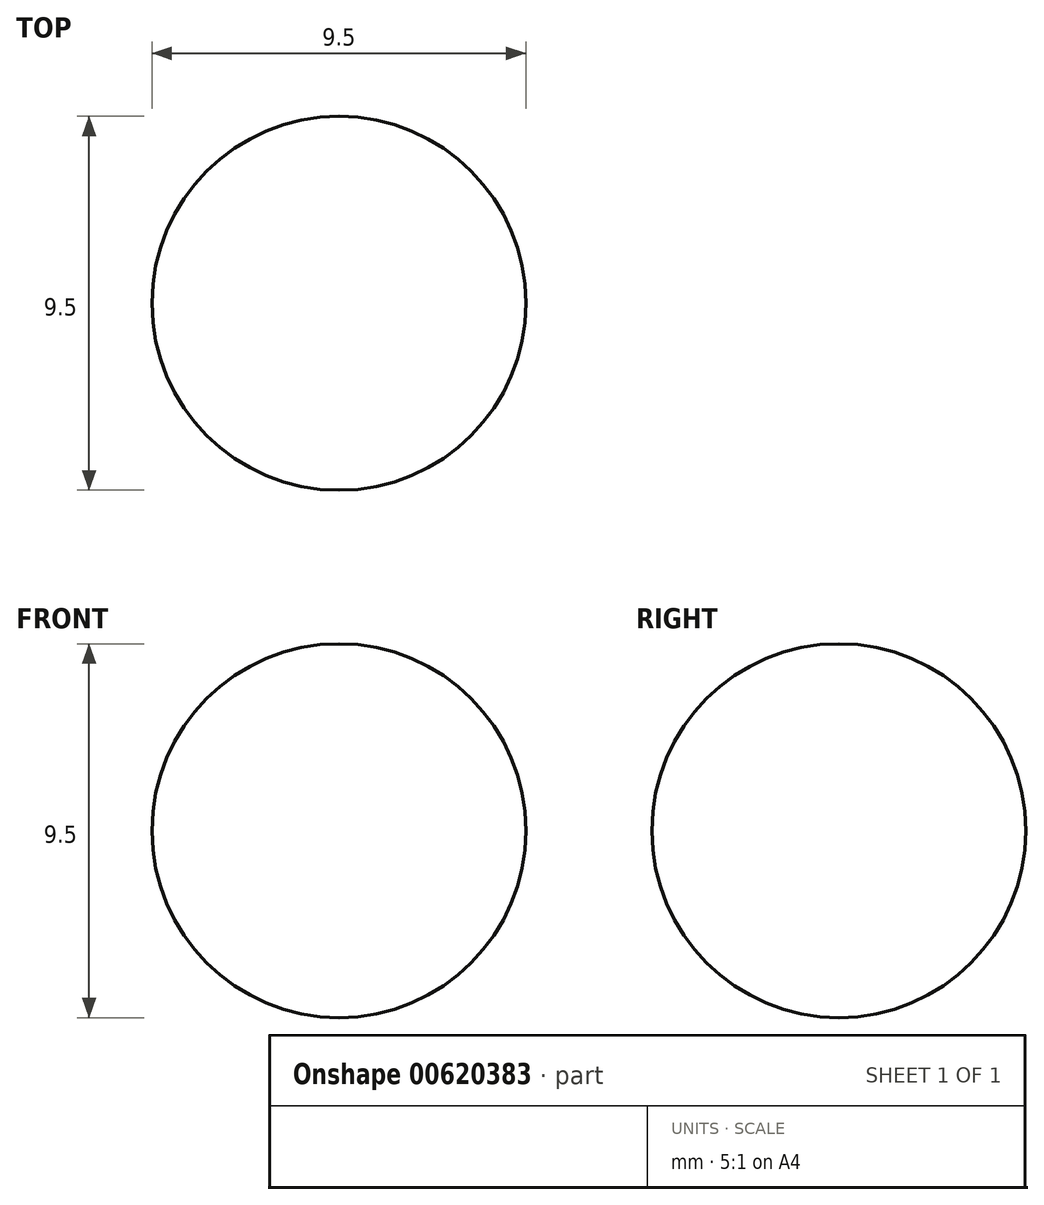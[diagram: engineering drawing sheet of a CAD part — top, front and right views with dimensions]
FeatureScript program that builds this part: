
annotation { "Feature Type Name" : "Feature", "Feature Type Description" : "" }
export const myFeature = defineFeature(function(context is Context, id is Id, definition is map)
    precondition{}
    {
        {
            var Q0;
            Q0=qCreatedBy(makeId("Top.planeOp"),FACE);
            var sketch = newSketch(context, id + "F0", { "sketchPlane" : qUnion([Q0])});
            skCircle(sketch, "E0", {"center": v(0, 0) * mm, "radius": 4.75 * mm});
            skLineSegment(sketch, "E1", {"start": v(-68.81, 0) * mm, "end": v(64.2, 0) * mm, "construction": true});
            skLineSegment(sketch, "E2", {"start": v(-4.75, 0) * mm, "end": v(4.75, 0) * mm});
            skSolve(sketch);
        }
        {
            var Q0;
            {var subQ0=sQuery(id+"F0.wireOp",EDGE,"E2");Q0=makeQuery(id+"F0.imprint","IMPRINT",FACE,{"disambiguationData":[TD([[makeQuery(id+"F0.imprint","IMPRINT",EDGE,{"derivedFrom":subQ0}),1.0]])]});}
            var Q1;
            Q1=sQuery(id+"F0.wireOp",EDGE,"E1");
            revolve(context, id + "F1", {"entities" : qUnion([Q0]), "axis" : qUnion([Q1]), "revolveType" : RevolveType.FULL});
        }
    });
